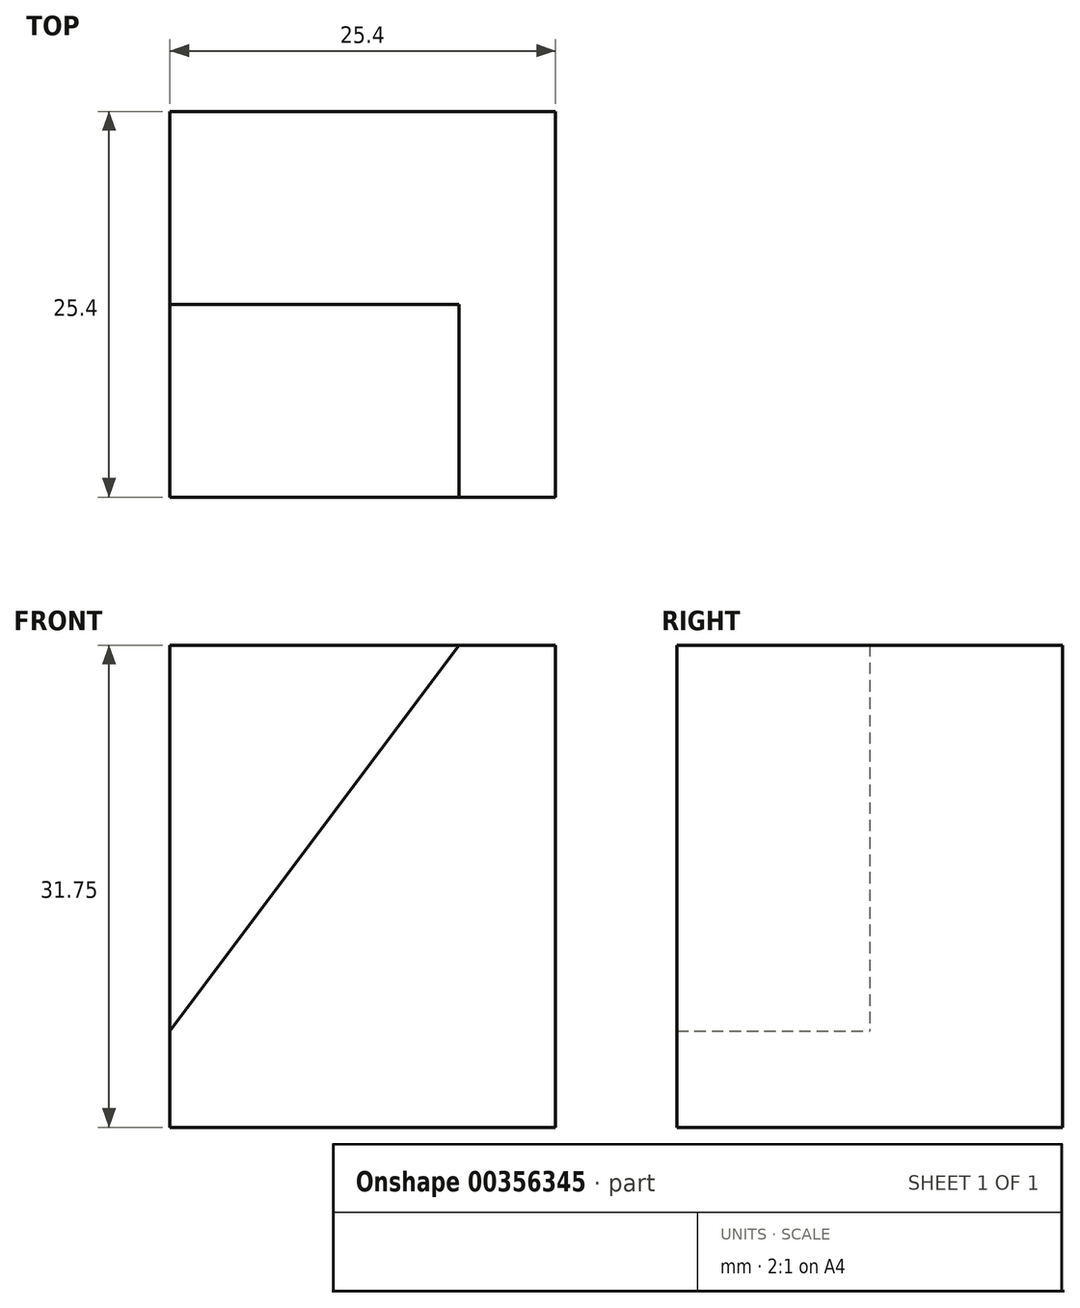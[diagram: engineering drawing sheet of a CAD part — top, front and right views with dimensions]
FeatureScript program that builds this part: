
annotation { "Feature Type Name" : "Feature", "Feature Type Description" : "" }
export const myFeature = defineFeature(function(context is Context, id is Id, definition is map)
    precondition{}
    {
        {
            var Q0;
            Q0=qCreatedBy(makeId("Front.planeOp"),FACE);
            var sketch = newSketch(context, id + "F0", { "sketchPlane" : qUnion([Q0])});
            skLineSegment(sketch, "E0", {"start": v(0, 0) * mm, "end": v(25.4, 0) * mm});
            skLineSegment(sketch, "E1", {"start": v(25.4, 0) * mm, "end": v(25.4, 31.75) * mm});
            skLineSegment(sketch, "E2", {"start": v(25.4, 31.75) * mm, "end": v(19.05, 31.75) * mm});
            skLineSegment(sketch, "E3", {"start": v(0, 0) * mm, "end": v(0, 6.35) * mm});
            skLineSegment(sketch, "E4", {"start": v(0, 6.35) * mm, "end": v(19.05, 31.75) * mm});
            skSolve(sketch);
        }
        {
            var Q0;
            Q0=makeQuery(id+"F0.imprint","IMPRINT",FACE,{"disambiguationData":[TD([[makeQuery(id+"F0.imprint","IMPRINT",EDGE,{"derivedFrom":sQuery(id+"F0.wireOp",EDGE,"E0")}),1.0]])]});
            extrude(context, id + "F1", {"entities" : qUnion([Q0]), "depth" : 25.4 * mm});
        }
        {
            var Q0;
            Q0=qCreatedBy(makeId("Front.planeOp"),FACE);
            var sketch = newSketch(context, id + "F2", { "sketchPlane" : qUnion([Q0])});
            skLineSegment(sketch, "E5", {"start": v(25.4, 31.75) * mm, "end": v(0, 31.75) * mm});
            skLineSegment(sketch, "E6", {"start": v(0, 31.75) * mm, "end": v(0, 0) * mm});
            skLineSegment(sketch, "E7", {"start": v(0, 0) * mm, "end": v(24.83, 0) * mm});
            skLineSegment(sketch, "E8", {"start": v(24.83, 0) * mm, "end": v(25.4, 31.75) * mm});
            skSolve(sketch);
        }
        {
            var Q0;
            Q0=makeQuery(id+"F2.imprint","IMPRINT",FACE,{"disambiguationData":[TD([[makeQuery(id+"F2.imprint","IMPRINT",EDGE,{"derivedFrom":sQuery(id+"F2.wireOp",EDGE,"E5")}),1.0]])]});
            extrude(context, id + "F3", {"entities" : qUnion([Q0]), "operationType" : NewBodyOperationType.ADD, "depth" : 12.7 * mm});
        }
    });
